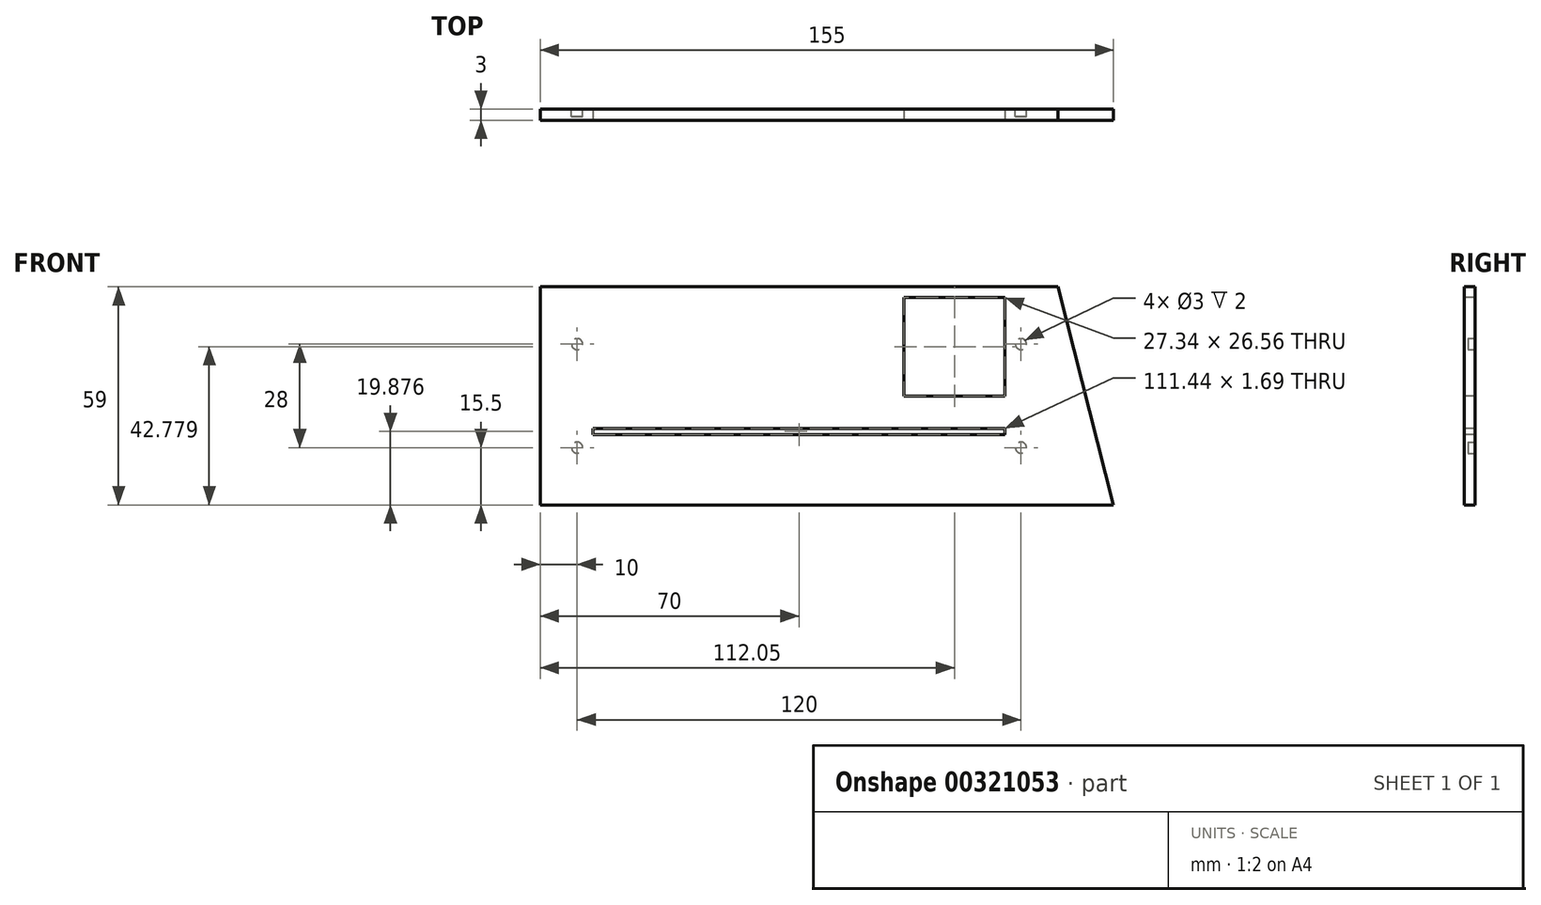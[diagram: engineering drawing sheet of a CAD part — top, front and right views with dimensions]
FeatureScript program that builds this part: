
annotation { "Feature Type Name" : "Feature", "Feature Type Description" : "" }
export const myFeature = defineFeature(function(context is Context, id is Id, definition is map)
    precondition{}
    {
        {
            var Q0;
            Q0=qCreatedBy(makeId("Front.planeOp"),FACE);
            var sketch = newSketch(context, id + "F0", { "sketchPlane" : qUnion([Q0])});
            skLineSegment(sketch, "E0.bottom", {"start": v(70, 29.5) * mm, "end": v(-70, 29.5) * mm});
            skLineSegment(sketch, "E0.top", {"start": v(70, -29.5) * mm, "end": v(-70, -29.5) * mm});
            skLineSegment(sketch, "E0.left", {"start": v(70, 29.5) * mm, "end": v(70, -29.5) * mm});
            skLineSegment(sketch, "E0.right", {"start": v(-70, 29.5) * mm, "end": v(-70, -29.5) * mm});
            skPoint(sketch, "E0.middle", {"position": v(0, 0) * mm});
            skLineSegment(sketch, "E1", {"start": v(70, 29.5) * mm, "end": v(85, -29.5) * mm});
            skLineSegment(sketch, "E2", {"start": v(85, -29.5) * mm, "end": v(70, -29.5) * mm});
            skSolve(sketch);
        }
        {
            var Q0;
            Q0 = qSketchRegion(id + "F0", true);
            extrude(context, id + "F1", {"entities" : qUnion([Q0]), "depth" : 3 * mm});
        }
        {
            var Q0;
            Q0=makeQuery(id+"F1.opExtrude","CAP_FACE",FACE,{"disambiguationData":[OSD([sQuery(id+"F0.wireOp",EDGE,"E0.bottom"),sQuery(id+"F0.wireOp",EDGE,"E0.top"),sQuery(id+"F0.wireOp",EDGE,"E0.right"),sQuery(id+"F0.wireOp",EDGE,"E1"),sQuery(id+"F0.wireOp",EDGE,"E2")])],"isStart":false});
            var sketch = newSketch(context, id + "F2", { "sketchPlane" : qUnion([Q0])});
            skLineSegment(sketch, "E3.bottom", {"start": v(55.72, -8.78) * mm, "end": v(-55.72, -8.78) * mm});
            skLineSegment(sketch, "E3.top", {"start": v(55.72, -10.47) * mm, "end": v(-55.72, -10.47) * mm});
            skLineSegment(sketch, "E3.left", {"start": v(55.72, -8.78) * mm, "end": v(55.72, -10.47) * mm});
            skLineSegment(sketch, "E3.right", {"start": v(-55.72, -8.78) * mm, "end": v(-55.72, -10.47) * mm});
            skPoint(sketch, "E3.middle", {"position": v(0, -9.62) * mm});
            skSolve(sketch);
        }
        {
            var Q0;
            Q0 = qSketchRegion(id + "F2", true);
            extrude(context, id + "F3", {"entities" : qUnion([Q0]), "operationType" : NewBodyOperationType.REMOVE, "oppositeDirection" : true, "depth" : 25 * mm});
        }
        {
            var Q0;
            Q0=makeQuery(id+"F1.opExtrude","CAP_FACE",FACE,{"disambiguationData":[OSD([sQuery(id+"F0.wireOp",EDGE,"E0.bottom"),sQuery(id+"F0.wireOp",EDGE,"E0.top"),sQuery(id+"F0.wireOp",EDGE,"E0.right"),sQuery(id+"F0.wireOp",EDGE,"E1"),sQuery(id+"F0.wireOp",EDGE,"E2")])],"isStart":false});
            var sketch = newSketch(context, id + "F4", { "sketchPlane" : qUnion([Q0])});
            skLineSegment(sketch, "E4.bottom", {"start": v(28.38, 22.22) * mm, "end": v(55.72, 22.22) * mm});
            skLineSegment(sketch, "E4.top", {"start": v(28.38, 3.22) * mm, "end": v(55.72, 3.22) * mm});
            skLineSegment(sketch, "E4.left", {"start": v(28.38, 22.22) * mm, "end": v(28.38, 3.22) * mm});
            skLineSegment(sketch, "E4.right", {"start": v(55.72, 22.22) * mm, "end": v(55.72, 3.22) * mm});
            skSolve(sketch);
        }
        {
            var Q0;
            Q0 = qSketchRegion(id + "F4", true);
            extrude(context, id + "F5", {"entities" : qUnion([Q0]), "operationType" : NewBodyOperationType.REMOVE, "oppositeDirection" : true, "depth" : 25 * mm});
        }
        {
            var Q0;
            Q0=makeQuery(id+"F1.opExtrude","CAP_FACE",FACE,{"disambiguationData":[OSD([sQuery(id+"F0.wireOp",EDGE,"E0.bottom"),sQuery(id+"F0.wireOp",EDGE,"E0.top"),sQuery(id+"F0.wireOp",EDGE,"E0.right"),sQuery(id+"F0.wireOp",EDGE,"E1"),sQuery(id+"F0.wireOp",EDGE,"E2")])],"isStart":true});
            var sketch = newSketch(context, id + "F6", { "sketchPlane" : qUnion([Q0])});
            skCircle(sketch, "E5", {"center": v(60, 14) * mm, "radius": 1.5 * mm});
            skCircle(sketch, "E6", {"center": v(-60, 14) * mm, "radius": 1.5 * mm});
            skCircle(sketch, "E7", {"center": v(60, -14) * mm, "radius": 1.5 * mm});
            skCircle(sketch, "E8", {"center": v(-60, -14) * mm, "radius": 1.5 * mm});
            skSolve(sketch);
        }
        {
            var Q0;
            Q0 = qSketchRegion(id + "F6", true);
            extrude(context, id + "F7", {"entities" : qUnion([Q0]), "operationType" : NewBodyOperationType.REMOVE, "oppositeDirection" : true, "depth" : 2 * mm});
        }
        {
            var Q0;
            Q0=makeQuery(id+"F1.opExtrude","CAP_FACE",FACE,{"disambiguationData":[OSD([sQuery(id+"F0.wireOp",EDGE,"E0.bottom"),sQuery(id+"F0.wireOp",EDGE,"E0.top"),sQuery(id+"F0.wireOp",EDGE,"E0.right"),sQuery(id+"F0.wireOp",EDGE,"E1"),sQuery(id+"F0.wireOp",EDGE,"E2")])],"isStart":false});
            var sketch = newSketch(context, id + "F8", { "sketchPlane" : qUnion([Q0])});
            skLineSegment(sketch, "E9.bottom", {"start": v(28.38, 26.56) * mm, "end": v(55.72, 26.56) * mm});
            skLineSegment(sketch, "E9.top", {"start": v(28.38, 0) * mm, "end": v(55.72, 0) * mm});
            skLineSegment(sketch, "E9.left", {"start": v(28.38, 26.56) * mm, "end": v(28.38, 0) * mm});
            skLineSegment(sketch, "E9.right", {"start": v(55.72, 26.56) * mm, "end": v(55.72, 0) * mm});
            skSolve(sketch);
        }
        {
            var Q0;
            Q0 = qSketchRegion(id + "F8", true);
            extrude(context, id + "F9", {"entities" : qUnion([Q0]), "operationType" : NewBodyOperationType.REMOVE, "oppositeDirection" : true, "depth" : 25 * mm});
        }
    });
